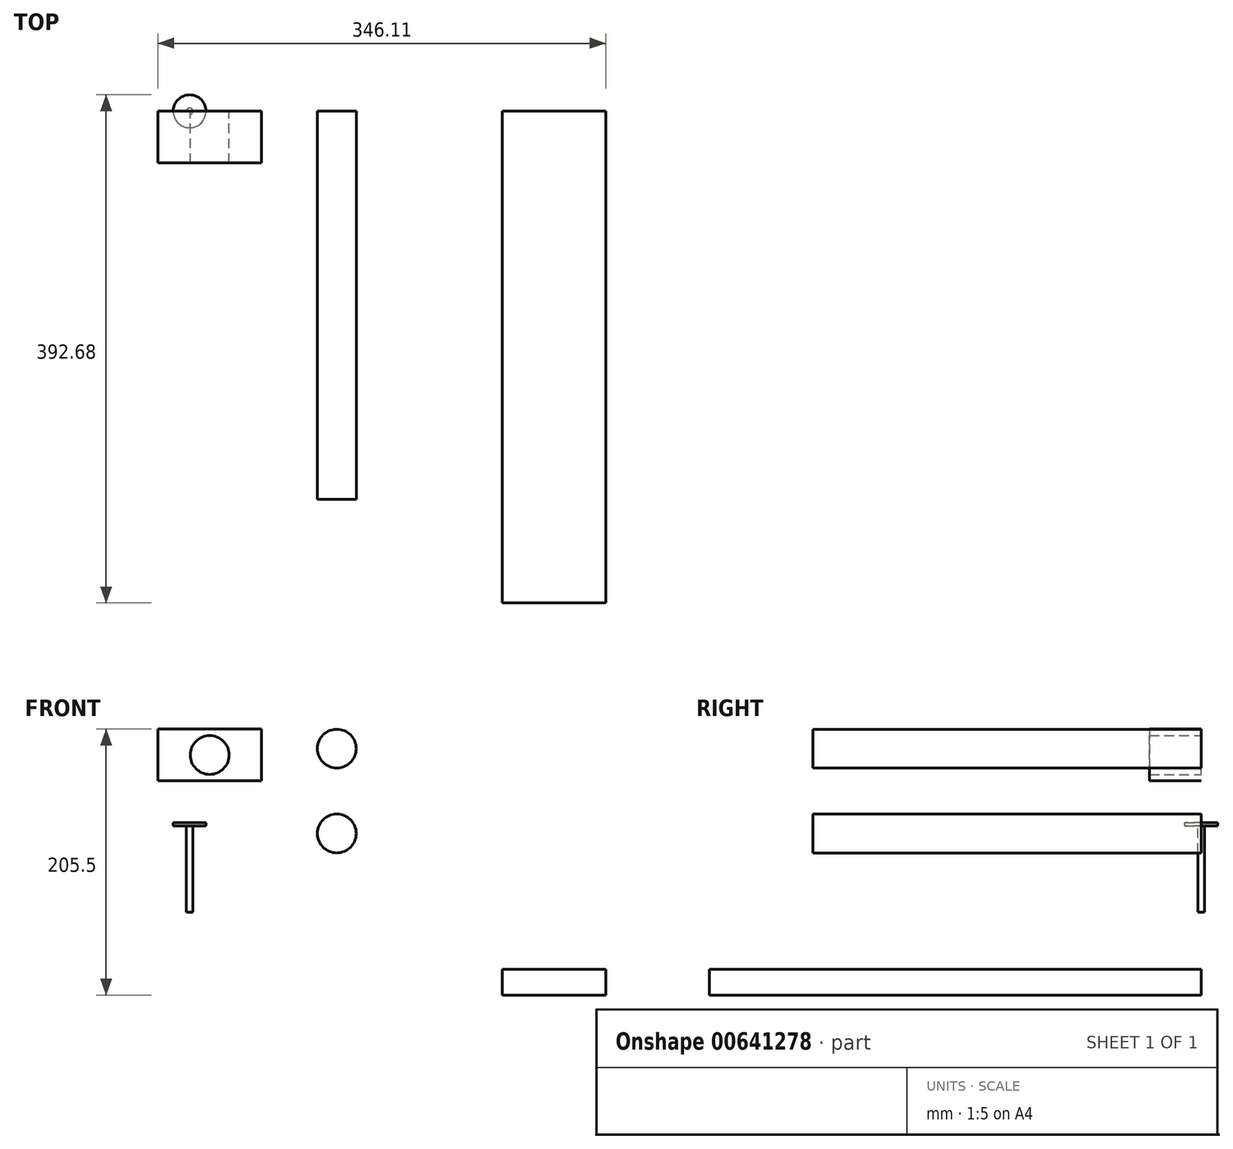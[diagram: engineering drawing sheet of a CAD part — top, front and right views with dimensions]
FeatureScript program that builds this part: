
annotation { "Feature Type Name" : "Feature", "Feature Type Description" : "" }
export const myFeature = defineFeature(function(context is Context, id is Id, definition is map)
    precondition{}
    {
        {
            var Q0;
            Q0=qCreatedBy(makeId("Front.planeOp"),FACE);
            var sketch = newSketch(context, id + "F0", { "sketchPlane" : qUnion([Q0])});
            skCircle(sketch, "E0", {"center": v(0, 45.77) * mm, "radius": 15 * mm});
            skCircle(sketch, "E1", {"center": v(0, -19.8) * mm, "radius": 15 * mm});
            skLineSegment(sketch, "E2.bottom", {"start": v(-138.19, 60.83) * mm, "end": v(-58.19, 60.83) * mm});
            skLineSegment(sketch, "E2.top", {"start": v(-138.19, 20.83) * mm, "end": v(-58.19, 20.83) * mm});
            skLineSegment(sketch, "E2.left", {"start": v(-138.19, 60.83) * mm, "end": v(-138.19, 20.83) * mm});
            skLineSegment(sketch, "E2.right", {"start": v(-58.19, 60.83) * mm, "end": v(-58.19, 20.83) * mm});
            skCircle(sketch, "E3", {"center": v(-98.19, 40.83) * mm, "radius": 15 * mm});
            skPoint(sketch, "E3.centerSnap0", {"position": v(-98.19, 60.83) * mm});
            skPoint(sketch, "E3.centerSnap1", {"position": v(-138.19, 40.83) * mm});
            skLineSegment(sketch, "E4", {"start": v(-113.67, -11.47) * mm, "end": v(-113.67, -80.64) * mm});
            skLineSegment(sketch, "E5", {"start": v(-113.67, -80.64) * mm, "end": v(-116.17, -80.64) * mm});
            skLineSegment(sketch, "E6", {"start": v(-116.17, -80.64) * mm, "end": v(-116.17, -13.97) * mm});
            skLineSegment(sketch, "E7", {"start": v(-116.17, -13.97) * mm, "end": v(-126.35, -13.97) * mm});
            skLineSegment(sketch, "E8", {"start": v(-126.35, -13.97) * mm, "end": v(-126.35, -11.47) * mm});
            skLineSegment(sketch, "E9", {"start": v(-126.35, -11.47) * mm, "end": v(-113.67, -11.47) * mm});
            skLineSegment(sketch, "E10.bottom", {"start": v(127.92, -124.67) * mm, "end": v(207.92, -124.67) * mm});
            skLineSegment(sketch, "E10.top", {"start": v(127.92, -144.67) * mm, "end": v(207.92, -144.67) * mm});
            skLineSegment(sketch, "E10.left", {"start": v(127.92, -124.67) * mm, "end": v(127.92, -144.67) * mm});
            skLineSegment(sketch, "E10.right", {"start": v(207.92, -124.67) * mm, "end": v(207.92, -144.67) * mm});
            skSolve(sketch);
        }
        {
            var Q0;
            Q0=makeQuery(id+"F0.imprint","IMPRINT",FACE,{"disambiguationData":[TD([[makeQuery(id+"F0.imprint","IMPRINT",EDGE,{"derivedFrom":sQuery(id+"F0.wireOp",EDGE,"E2.bottom")}),-1.0]])]});
            extrude(context, id + "F1", {"entities" : qUnion([Q0]), "depth" : 40 * mm, "offsetDistance" : 25 * mm});
        }
        {
            var Q0;
            Q0=makeQuery(id+"F0.imprint","IMPRINT",FACE,{"disambiguationData":[TD([[makeQuery(id+"F0.imprint","IMPRINT",EDGE,{"derivedFrom":sQuery(id+"F0.wireOp",EDGE,"E0")}),1.0]])]});
            var Q1;
            Q1=makeQuery(id+"F0.imprint","IMPRINT",FACE,{"disambiguationData":[TD([[makeQuery(id+"F0.imprint","IMPRINT",EDGE,{"derivedFrom":sQuery(id+"F0.wireOp",EDGE,"E1")}),1.0]])]});
            extrude(context, id + "F2", {"entities" : qUnion([Q0, Q1]), "depth" : 300 * mm, "offsetDistance" : 25 * mm});
        }
        {
            var Q0;
            Q0=makeQuery(id+"F0.imprint","IMPRINT",FACE,{"disambiguationData":[TD([[makeQuery(id+"F0.imprint","IMPRINT",EDGE,{"derivedFrom":sQuery(id+"F0.wireOp",EDGE,"E4")}),-1.0]])]});
            var Q1;
            Q1=sQuery(id+"F0.wireOp",EDGE,"E4");
            revolve(context, id + "F3", {"entities" : qUnion([Q0]), "axis" : qUnion([Q1]), "revolveType" : RevolveType.FULL});
        }
        {
            var Q0;
            Q0=makeQuery(id+"F0.imprint","IMPRINT",FACE,{"disambiguationData":[TD([[makeQuery(id+"F0.imprint","IMPRINT",EDGE,{"derivedFrom":sQuery(id+"F0.wireOp",EDGE,"E10.bottom")}),-1.0]])]});
            extrude(context, id + "F4", {"entities" : qUnion([Q0]), "depth" : 380 * mm, "offsetDistance" : 25 * mm});
        }
        {
            var Q0;
            Q0=makeQuery(id+"F4.opExtrude","SWEPT_FACE",FACE,{"disambiguationData":[OSD([sQuery(id+"F0.wireOp",EDGE,"E10.bottom")])]});
            var sketch = newSketch(context, id + "F5", { "sketchPlane" : qUnion([Q0])});
            skLineSegment(sketch, "E11", {"start": v(127.92, -40) * mm, "end": v(207.92, -40) * mm});
            skLineSegment(sketch, "E12", {"start": v(127.92, -340) * mm, "end": v(207.92, -340) * mm});
            skSolve(sketch);
        }
    });
